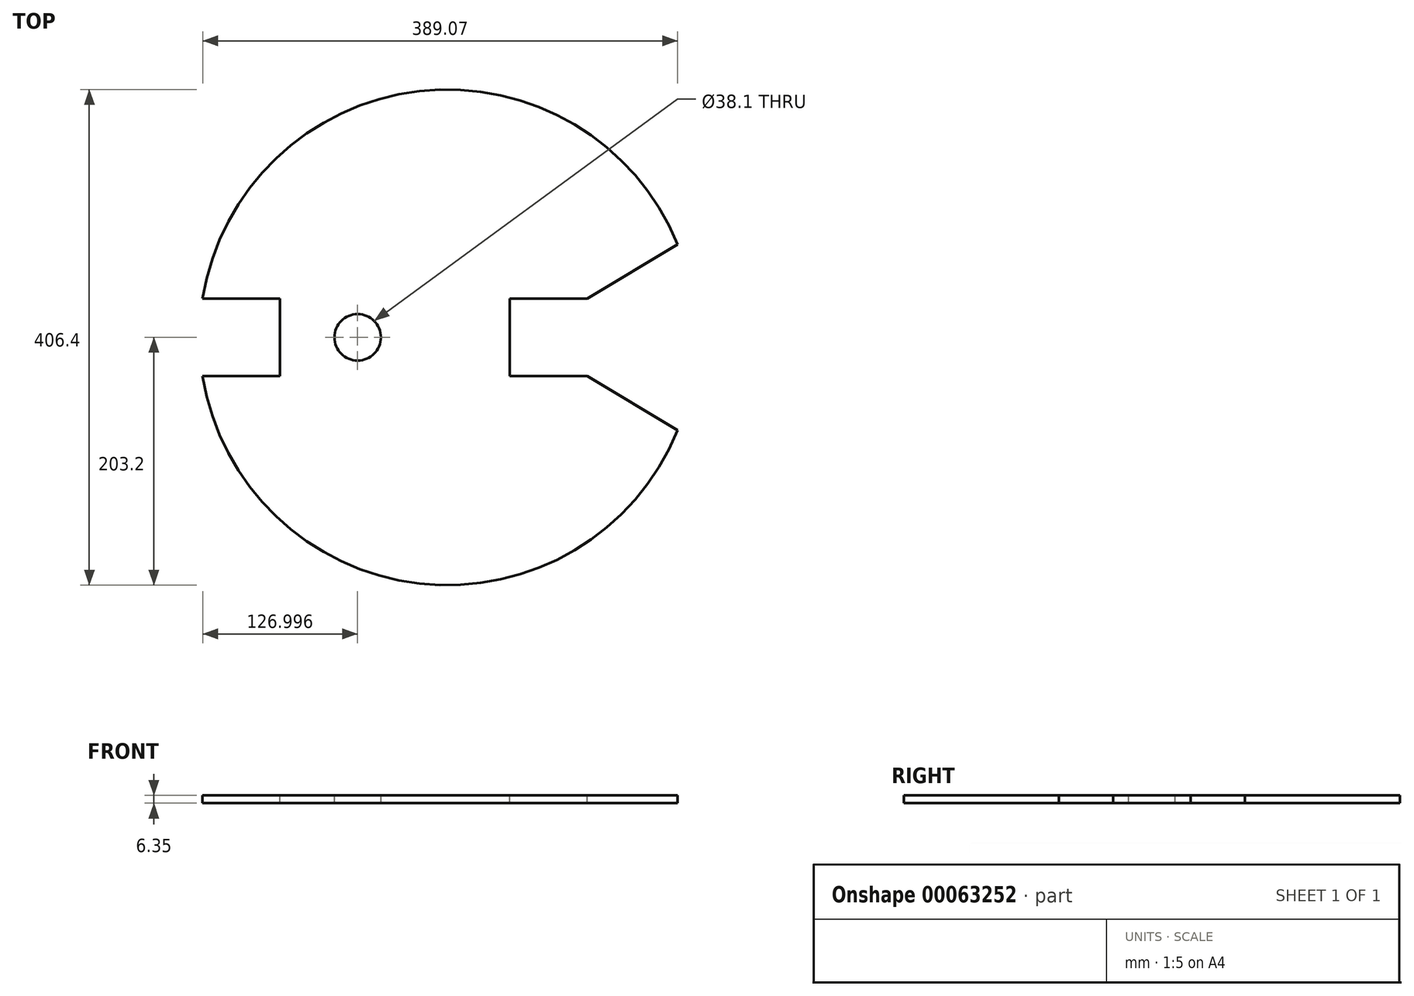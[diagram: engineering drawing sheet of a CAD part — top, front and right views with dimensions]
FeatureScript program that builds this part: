
annotation { "Feature Type Name" : "Feature", "Feature Type Description" : "" }
export const myFeature = defineFeature(function(context is Context, id is Id, definition is map)
    precondition{}
    {
        {
            var Q0;
            Q0=qCreatedBy(makeId("Top.planeOp"),FACE);
            var sketch = newSketch(context, id + "F0", { "sketchPlane" : qUnion([Q0])});
            skCircle(sketch, "E0", {"center": v(0, 0) * mm, "radius": 203.2 * mm});
            skSolve(sketch);
        }
        {
            var Q0;
            Q0 = qSketchRegion(id + "F0", true);
            extrude(context, id + "F1", {"entities" : qUnion([Q0]), "depth" : 6.35 * mm});
        }
        {
            var Q0;
            Q0=makeQuery(id+"F1.opExtrude","CAP_FACE",FACE,{"disambiguationData":[OSD([sQuery(id+"F0.wireOp",EDGE,"E0")])],"isStart":false});
            var sketch = newSketch(context, id + "F2", { "sketchPlane" : qUnion([Q0])});
            skLineSegment(sketch, "E1.bottom", {"start": v(-200.7, -31.75) * mm, "end": v(-137.2, -31.75) * mm});
            skLineSegment(sketch, "E1.top", {"start": v(-200.7, 31.75) * mm, "end": v(-137.2, 31.75) * mm});
            skLineSegment(sketch, "E1.left", {"start": v(-200.7, -31.75) * mm, "end": v(-200.7, 31.75) * mm, "construction": true});
            skLineSegment(sketch, "E1.right", {"start": v(-137.2, -31.75) * mm, "end": v(-137.2, 31.75) * mm});
            skArc(sketch, "E2", {"start": v(-200.7, 31.75) * mm, "mid": v(-203.2, 0) * mm, "end": v(-200.7, -31.75) * mm});
            skSolve(sketch);
        }
        {
            var Q0;
            Q0 = qSketchRegion(id + "F2", true);
            extrude(context, id + "F3", {"entities" : qUnion([Q0]), "operationType" : NewBodyOperationType.REMOVE, "endBound" : BoundingType.THROUGH_ALL, "oppositeDirection" : true, "depth" : 25.4 * mm});
        }
        {
            var Q0;
            Q0=makeQuery(id+"F1.opExtrude","CAP_FACE",FACE,{"disambiguationData":[OSD([sQuery(id+"F0.wireOp",EDGE,"E0")])],"isStart":false});
            var sketch = newSketch(context, id + "F4", { "sketchPlane" : qUnion([Q0])});
            skLineSegment(sketch, "E3.bottom", {"start": v(50.8, -31.75) * mm, "end": v(203.2, -31.75) * mm, "construction": true});
            skLineSegment(sketch, "E3.top", {"start": v(50.8, 31.75) * mm, "end": v(203.2, 31.75) * mm, "construction": true});
            skLineSegment(sketch, "E3.left", {"start": v(50.8, -31.75) * mm, "end": v(50.8, 31.75) * mm});
            skLineSegment(sketch, "E3.right", {"start": v(203.2, -31.75) * mm, "end": v(203.2, 31.75) * mm, "construction": true});
            skLineSegment(sketch, "E4", {"start": v(0, 0) * mm, "end": v(203.2, 0) * mm, "construction": true});
            skLineSegment(sketch, "E5", {"start": v(114.3, -31.75) * mm, "end": v(188.37, -76.2) * mm});
            skLineSegment(sketch, "E6", {"start": v(114.3, 31.75) * mm, "end": v(188.37, 76.2) * mm});
            skLineSegment(sketch, "E7", {"start": v(114.3, -31.75) * mm, "end": v(114.3, 31.75) * mm, "construction": true});
            skArc(sketch, "E8", {"start": v(188.37, -76.2) * mm, "mid": v(203.2, 0) * mm, "end": v(188.37, 76.2) * mm});
            skLineSegment(sketch, "E9", {"start": v(188.37, -76.2) * mm, "end": v(188.37, 76.2) * mm});
            skLineSegment(sketch, "E10", {"start": v(50.8, -31.75) * mm, "end": v(114.3, -31.75) * mm});
            skLineSegment(sketch, "E11", {"start": v(50.8, 31.75) * mm, "end": v(114.3, 31.75) * mm});
            skSolve(sketch);
        }
        {
            var Q0;
            Q0 = qSketchRegion(id + "F4", true);
            extrude(context, id + "F5", {"entities" : qUnion([Q0]), "operationType" : NewBodyOperationType.REMOVE, "endBound" : BoundingType.THROUGH_ALL, "oppositeDirection" : true, "depth" : 25.4 * mm});
        }
        {
            var Q0;
            Q0=makeQuery(id+"F1.opExtrude","CAP_FACE",FACE,{"disambiguationData":[OSD([sQuery(id+"F0.wireOp",EDGE,"E0")])],"isStart":false});
            var sketch = newSketch(context, id + "F6", { "sketchPlane" : qUnion([Q0])});
            skCircle(sketch, "E12", {"center": v(-73.7, 0) * mm, "radius": 19.05 * mm});
            skLineSegment(sketch, "E13", {"start": v(-137.2, 0) * mm, "end": v(-73.7, 0) * mm, "construction": true});
            skSolve(sketch);
        }
        {
            var Q0;
            Q0 = qSketchRegion(id + "F6", true);
            extrude(context, id + "F7", {"entities" : qUnion([Q0]), "operationType" : NewBodyOperationType.REMOVE, "endBound" : BoundingType.THROUGH_ALL, "oppositeDirection" : true, "depth" : 25.4 * mm});
        }
    });
